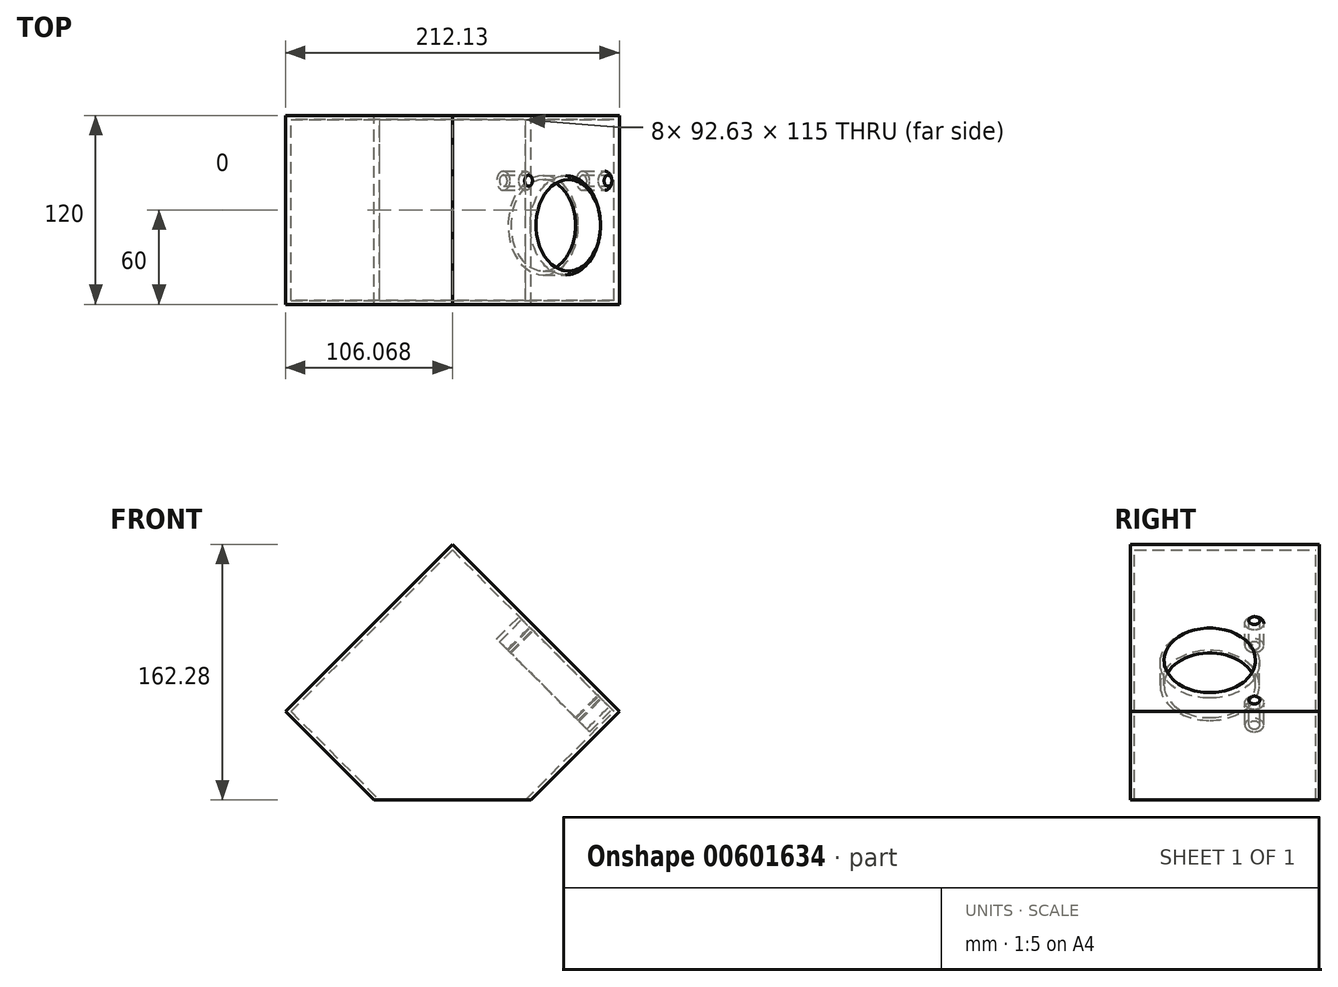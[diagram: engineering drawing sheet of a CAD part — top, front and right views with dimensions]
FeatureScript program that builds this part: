
annotation { "Feature Type Name" : "Feature", "Feature Type Description" : "" }
export const myFeature = defineFeature(function(context is Context, id is Id, definition is map)
    precondition{}
    {
        {
            var Q0;
            Q0=qCreatedBy(makeId("Front.planeOp"),FACE);
            var sketch = newSketch(context, id + "F0", { "sketchPlane" : qUnion([Q0])});
            skLineSegment(sketch, "E0", {"start": v(65.03, 0) * mm, "end": v(121.24, 56.22) * mm});
            skLineSegment(sketch, "E1", {"start": v(121.24, 56.22) * mm, "end": v(15.18, 162.28) * mm});
            skLineSegment(sketch, "E2", {"start": v(15.18, 162.28) * mm, "end": v(-90.89, 56.22) * mm});
            skLineSegment(sketch, "E3", {"start": v(-90.89, 56.22) * mm, "end": v(-34.67, 0) * mm});
            skLineSegment(sketch, "E4", {"start": v(-34.67, 0) * mm, "end": v(65.03, 0) * mm});
            skSolve(sketch);
        }
        {
            var Q0;
            Q0=makeQuery(id+"F0.imprint","IMPRINT",FACE,{"disambiguationData":[TD([[makeQuery(id+"F0.imprint","IMPRINT",EDGE,{"derivedFrom":sQuery(id+"F0.wireOp",EDGE,"E0")}),1.0]])]});
            extrude(context, id + "F1", {"entities" : qUnion([Q0]), "endBound" : BoundingType.SYMMETRIC, "depth" : 120 * mm});
        }
        {
            var Q0;
            Q0=makeQuery(id+"F1.opExtrude","SWEPT_FACE",FACE,{"disambiguationData":[OSD([sQuery(id+"F0.wireOp",EDGE,"E1")])]});
            var sketch = newSketch(context, id + "F2", { "sketchPlane" : qUnion([Q0])});
            skLineSegment(sketch, "E5.bottom", {"start": v(24.06, 43.2) * mm, "end": v(-80.44, 43.2) * mm});
            skLineSegment(sketch, "E5.top", {"start": v(24.06, -43.2) * mm, "end": v(-80.44, -43.2) * mm});
            skLineSegment(sketch, "E5.left", {"start": v(26.06, 41.2) * mm, "end": v(26.06, -41.2) * mm});
            skLineSegment(sketch, "E5.right", {"start": v(-82.44, 41.2) * mm, "end": v(-82.44, -41.2) * mm});
            skPoint(sketch, "E5.middle", {"position": v(-28.19, 0) * mm});
            skPoint(sketch, "E6.visualSharp", {"position": v(-82.44, -43.2) * mm});
            skArc(sketch, "E6.filletArc", {"start": v(-82.44, -41.2) * mm, "mid": v(-81.85, -42.61) * mm, "end": v(-80.44, -43.2) * mm});
            skPoint(sketch, "E7.visualSharp", {"position": v(-82.44, 43.2) * mm});
            skArc(sketch, "E7.filletArc", {"start": v(-80.44, 43.2) * mm, "mid": v(-81.85, 42.61) * mm, "end": v(-82.44, 41.2) * mm});
            skPoint(sketch, "E8.visualSharp", {"position": v(26.06, 43.2) * mm});
            skArc(sketch, "E8.filletArc", {"start": v(26.06, 41.2) * mm, "mid": v(25.48, 42.61) * mm, "end": v(24.06, 43.2) * mm});
            skPoint(sketch, "E9.visualSharp", {"position": v(26.06, -43.2) * mm});
            skArc(sketch, "E9.filletArc", {"start": v(24.06, -43.2) * mm, "mid": v(25.48, -42.61) * mm, "end": v(26.06, -41.2) * mm});
            skCircle(sketch, "E10", {"center": v(-9.74, 0) * mm, "radius": 29 * mm});
            skCircle(sketch, "E11", {"center": v(-74.94, -35.7) * mm, "radius": 3.5 * mm});
            skCircle(sketch, "E12", {"center": v(-74.94, 35.7) * mm, "radius": 3.5 * mm});
            skCircle(sketch, "E13", {"center": v(18.56, 35.7) * mm, "radius": 3.5 * mm});
            skCircle(sketch, "E14", {"center": v(18.56, -35.7) * mm, "radius": 3.5 * mm});
            skSolve(sketch);
        }
        {
            var Q0;
            Q0=makeQuery(id+"F2.imprint","IMPRINT",FACE,{"disambiguationData":[TD([[makeQuery(id+"F2.imprint","IMPRINT",EDGE,{"derivedFrom":sQuery(id+"F2.wireOp",EDGE,"E5.bottom")}),1.0]])]});
            var Q1;
            Q1=makeQuery(id+"F2.imprint","IMPRINT",FACE,{"disambiguationData":[TD([[makeQuery(id+"F2.imprint","IMPRINT",EDGE,{"derivedFrom":sQuery(id+"F2.wireOp",EDGE,"E10")}),1.0]])]});
            var Q2;
            Q2=makeQuery(id+"F2.imprint","IMPRINT",FACE,{"disambiguationData":[TD([[makeQuery(id+"F2.imprint","IMPRINT",EDGE,{"derivedFrom":sQuery(id+"F2.wireOp",EDGE,"E11")}),1.0]])]});
            var Q3;
            Q3=makeQuery(id+"F2.imprint","IMPRINT",FACE,{"disambiguationData":[TD([[makeQuery(id+"F2.imprint","IMPRINT",EDGE,{"derivedFrom":sQuery(id+"F2.wireOp",EDGE,"E12")}),1.0]])]});
            var Q4;
            Q4=makeQuery(id+"F2.imprint","IMPRINT",FACE,{"disambiguationData":[TD([[makeQuery(id+"F2.imprint","IMPRINT",EDGE,{"derivedFrom":sQuery(id+"F2.wireOp",EDGE,"E13")}),1.0]])]});
            var Q5;
            Q5=makeQuery(id+"F2.imprint","IMPRINT",FACE,{"disambiguationData":[TD([[makeQuery(id+"F2.imprint","IMPRINT",EDGE,{"derivedFrom":sQuery(id+"F2.wireOp",EDGE,"E14")}),1.0]])]});
            extrude(context, id + "F3", {"entities" : qUnion([Q0, Q1, Q2, Q3, Q4, Q5]), "operationType" : NewBodyOperationType.REMOVE, "oppositeDirection" : true, "depth" : 20 * mm});
        }
        {
            var Q0;
            Q0=makeQuery(id+"F1.opExtrude","SWEPT_FACE",FACE,{"disambiguationData":[OSD([sQuery(id+"F0.wireOp",EDGE,"E4")])]});
            shell(context, id + "F4", {"entities" : qUnion([Q0]), "thickness" : 2.5 * mm});
        }
        {
            var Q0;
            Q0=makeQuery(id+"F2.imprint","IMPRINT",FACE,{"disambiguationData":[TD([[makeQuery(id+"F2.imprint","IMPRINT",EDGE,{"derivedFrom":sQuery(id+"F2.wireOp",EDGE,"E10")}),1.0]])]});
            var Q1;
            Q1=makeQuery(id+"F2.imprint","IMPRINT",FACE,{"disambiguationData":[TD([[makeQuery(id+"F2.imprint","IMPRINT",EDGE,{"derivedFrom":sQuery(id+"F2.wireOp",EDGE,"E12")}),1.0]])]});
            var Q2;
            Q2=makeQuery(id+"F2.imprint","IMPRINT",FACE,{"disambiguationData":[TD([[makeQuery(id+"F2.imprint","IMPRINT",EDGE,{"derivedFrom":sQuery(id+"F2.wireOp",EDGE,"E11")}),1.0]])]});
            var Q3;
            Q3=makeQuery(id+"F2.imprint","IMPRINT",FACE,{"disambiguationData":[TD([[makeQuery(id+"F2.imprint","IMPRINT",EDGE,{"derivedFrom":sQuery(id+"F2.wireOp",EDGE,"E14")}),1.0]])]});
            var Q4;
            Q4=makeQuery(id+"F2.imprint","IMPRINT",FACE,{"disambiguationData":[TD([[makeQuery(id+"F2.imprint","IMPRINT",EDGE,{"derivedFrom":sQuery(id+"F2.wireOp",EDGE,"E13")}),1.0]])]});
            extrude(context, id + "F5", {"entities" : qUnion([Q0, Q1, Q2, Q3, Q4]), "operationType" : NewBodyOperationType.REMOVE, "oppositeDirection" : true, "depth" : 40 * mm});
        }
    });
